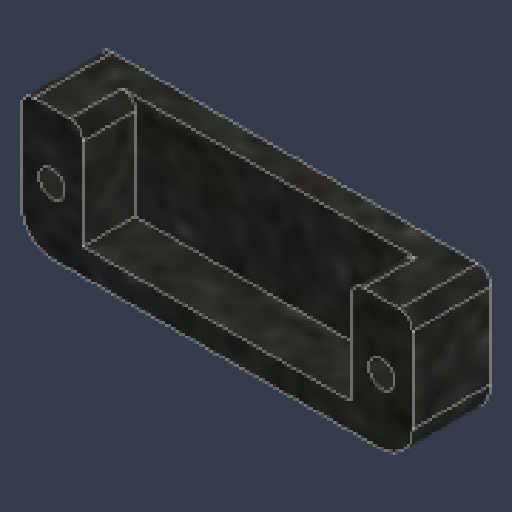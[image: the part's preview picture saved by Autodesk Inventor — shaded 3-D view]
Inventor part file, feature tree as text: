
AUTODESK INVENTOR PART (.ipt)
format: ipt  version: 2023.4 (Build 274418000, 418)  size: 148,992 bytes
history: native  units: mm
features: sketch x3, extrude x2, fillet x2, hole x1
ambient origin geometry x8: Origin, YZ Plane, XZ Plane, XY Plane, X Axis, Y Axis, Z Axis, Center Point
bodies: Solid1 (feature_tree)
feature tree (8):
  extrude  "Extrusion1"  Depth=20.0mm
  extrude  "Extrusion2"  Depth=41.0mm
  hole  "Hole1"  [1 undecoded]
  fillet  "Fillet1"  Radius=9.5mm
  fillet  "Fillet2"  Radius=4.75mm
  sketch  "Sketch1"  dims[d0=60.0mm d1=20.0mm]
  sketch  "Sketch2"  dims[d2=12.0mm d3=0.0mm d4=41.0mm]
  sketch  "Sketch3"  dims[d5=4.0mm d6=8.0mm d7=0.0mm d8=9.5mm d9=4.75mm d10=4.0mm d11=6.0mm d12=7.5mm d13=2.0mm d14=90.0deg d15=8.0mm d16=20.594885mm d17=2.0mm d18=5.0mm]
note: 1 required parameter value undecoded (feature->parameter linkage not recoverable at this tier; creation-order binding heuristic only, values carry confidence <= 0.55)
